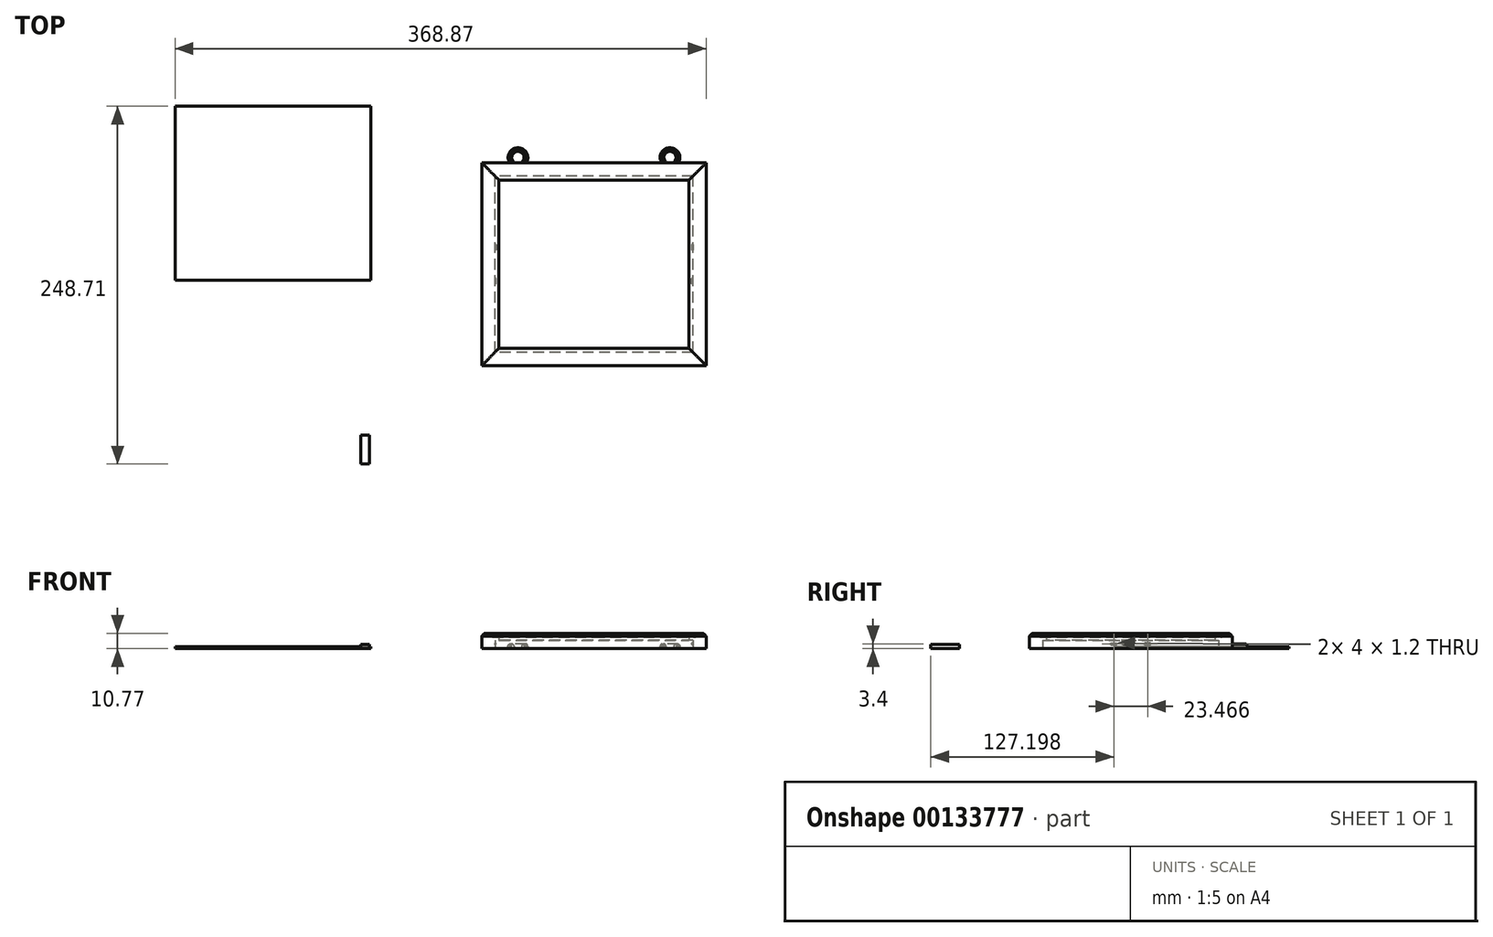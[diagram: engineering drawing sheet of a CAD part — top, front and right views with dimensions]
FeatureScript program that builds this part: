
annotation { "Feature Type Name" : "Feature", "Feature Type Description" : "" }
export const myFeature = defineFeature(function(context is Context, id is Id, definition is map)
    precondition{}
    {
        {
            var Q0;
            Q0=qCreatedBy(makeId("Top.planeOp"),FACE);
            var sketch = newSketch(context, id + "F0", { "sketchPlane" : qUnion([Q0])});
            skLineSegment(sketch, "E0.bottom", {"start": v(-66.53, 85.7) * mm, "end": v(11.47, 85.7) * mm});
            skLineSegment(sketch, "E0.top", {"start": v(-66.53, -55.3) * mm, "end": v(11.47, -55.3) * mm});
            skLineSegment(sketch, "E0.left", {"start": v(-66.53, 85.7) * mm, "end": v(-66.53, -55.3) * mm});
            skLineSegment(sketch, "E1.bottom", {"start": v(-54.53, 73.7) * mm, "end": v(11.47, 73.7) * mm});
            skLineSegment(sketch, "E1.top", {"start": v(-54.53, -43.3) * mm, "end": v(11.47, -43.3) * mm});
            skLineSegment(sketch, "E1.left", {"start": v(-54.53, 73.7) * mm, "end": v(-54.53, -43.3) * mm});
            skLineSegment(sketch, "E2", {"start": v(11.47, 73.7) * mm, "end": v(11.47, 85.7) * mm, "construction": true});
            skPoint(sketch, "E2.endSnap0", {"position": v(-27.53, 85.7) * mm});
            skLineSegment(sketch, "E3", {"start": v(11.47, -43.3) * mm, "end": v(11.47, -55.3) * mm, "construction": true});
            skLineSegment(sketch, "E4", {"start": v(-66.53, 15.2) * mm, "end": v(-54.53, 15.2) * mm, "construction": true});
            skLineSegment(sketch, "E5", {"start": v(11.47, 85.7) * mm, "end": v(11.47, -55.3) * mm});
            skSolve(sketch);
        }
        {
            var Q0;
            Q0=makeQuery(id+"F0.imprint","IMPRINT",FACE,{"disambiguationData":[TD([[makeQuery(id+"F0.imprint","IMPRINT",EDGE,{"derivedFrom":sQuery(id+"F0.wireOp",EDGE,"E0.bottom")}),-1.0]])]});
            extrude(context, id + "F1", {"entities" : qUnion([Q0]), "depth" : 11 * mm});
        }
        {
            var Q0;
            {var subQ0=sQuery(id+"F0.wireOp",EDGE,"E5");Q0=makeQuery(id+"F1.opExtrude","SWEPT_FACE",FACE,{"disambiguationData":[OSD([subQ0]),TDD([makeQuery(id+"F0.imprint","IMPRINT",EDGE,{"disambiguationData":[TD([[makeQuery(id+"F0.imprint","INTERSECT",VERTEX,{"derivedFrom":[sQuery(id+"F0.wireOp",EDGE,"E0.top"),subQ0]}),1.0]])],"derivedFrom":subQ0})])]});}
            var sketch = newSketch(context, id + "F2", { "sketchPlane" : qUnion([Q0])});
            skPoint(sketch, "E6.orphan", {"position": v(-55.3, 0) * mm});
            skPoint(sketch, "E7.orphan", {"position": v(-43.3, 0) * mm});
            skLineSegment(sketch, "E8.0", {"start": v(-43.3, 11) * mm, "end": v(-43.3, 9.78) * mm});
            skLineSegment(sketch, "E8.1", {"start": v(-43.3, 11) * mm, "end": v(-55.3, 11) * mm});
            skLineSegment(sketch, "E8.2", {"start": v(-55.3, 11) * mm, "end": v(-55.3, 8.58) * mm});
            skFitSpline(sketch, "E9", {"points": [v(-55.3, 8.58) * mm, v(-52.44, 10.76) * mm, v(-48.85, 8.44) * mm, v(-46.04, 8.62) * mm, v(-43.3, 9.78) * mm, v(-43.3, 9.83) * mm], "startDerivative": vector(9.21, 12.44) * mm, "endDerivative": vector(-0.8, 1.4) * mm});
            skSolve(sketch);
        }
        {
            var Q0;
            {var subQ0=sQuery(id+"F2.wireOp",EDGE,"E8.1");var subQ1=sQuery(id+"F2.wireOp",EDGE,"E8.0");var subQ2=makeQuery(id+"F2.imprint","INTERSECT",VERTEX,{"derivedFrom":[subQ1,subQ0]});Q0=makeQuery(id+"F2.imprint","IMPRINT",FACE,{"disambiguationData":[TD([[makeQuery(id+"F2.imprint","IMPRINT",EDGE,{"disambiguationData":[TD([[subQ2,-1.0]])],"derivedFrom":subQ1}),-1.0]])]});}
            var Q1;
            {var subQ0=sQuery(id+"F2.wireOp",EDGE,"E8.2");Q1=makeQuery(id+"F2.imprint","IMPRINT",FACE,{"disambiguationData":[TD([[makeQuery(id+"F2.imprint","IMPRINT",EDGE,{"derivedFrom":subQ0}),1.0]])]});}
            var Q2;
            Q2=makeQuery(id+"F1.opExtrude","CAP_EDGE",EDGE,{"disambiguationData":[OSD([sQuery(id+"F0.wireOp",EDGE,"E0.top")])],"isStart":false});
            var Q3;
            Q3=makeQuery(id+"F1.opExtrude","CAP_EDGE",EDGE,{"disambiguationData":[OSD([sQuery(id+"F0.wireOp",EDGE,"E0.left")])],"isStart":false});
            var Q4;
            Q4=makeQuery(id+"F1.opExtrude","CAP_EDGE",EDGE,{"disambiguationData":[OSD([sQuery(id+"F0.wireOp",EDGE,"E0.bottom")])],"isStart":false});
            sweep(context, id + "F3", {"operationType" : NewBodyOperationType.REMOVE, "profiles" : qUnion([Q0, Q1]), "path" : qUnion([Q2, Q3, Q4])});
        }
        {
            var Q0;
            Q0=makeQuery(id+"F1.opExtrude","CAP_FACE",FACE,{"disambiguationData":[OSD([sQuery(id+"F0.wireOp",EDGE,"E0.bottom"),sQuery(id+"F0.wireOp",EDGE,"E0.top"),sQuery(id+"F0.wireOp",EDGE,"E0.left"),sQuery(id+"F0.wireOp",EDGE,"E1.bottom"),sQuery(id+"F0.wireOp",EDGE,"E1.top"),sQuery(id+"F0.wireOp",EDGE,"E1.left"),sQuery(id+"F0.wireOp",EDGE,"E5")])],"isStart":true});
            var sketch = newSketch(context, id + "F4", { "sketchPlane" : qUnion([Q0])});
            skLineSegment(sketch, "E10.bottom", {"start": v(11.47, 46) * mm, "end": v(-57.23, 46) * mm});
            skLineSegment(sketch, "E10.top", {"start": v(11.47, -76.4) * mm, "end": v(-57.23, -76.4) * mm});
            skLineSegment(sketch, "E10.left", {"start": v(11.47, 46) * mm, "end": v(11.47, -76.4) * mm});
            skLineSegment(sketch, "E10.right", {"start": v(-57.23, 46) * mm, "end": v(-57.23, -76.4) * mm});
            skLineSegment(sketch, "E11", {"start": v(-50.93, 43.3) * mm, "end": v(-50.93, 46) * mm, "construction": true});
            skLineSegment(sketch, "E12", {"start": v(-54.53, 8.71) * mm, "end": v(-57.23, 8.71) * mm, "construction": true});
            skLineSegment(sketch, "E13", {"start": v(-42.3, -73.7) * mm, "end": v(-42.3, -76.4) * mm, "construction": true});
            skSolve(sketch);
        }
        {
            var Q0;
            {var subQ7=sQuery(id+"F4.wireOp",EDGE,"E10.bottom");Q0=makeQuery(id+"F4.imprint","IMPRINT",FACE,{"disambiguationData":[TD([[makeQuery(id+"F4.imprint","IMPRINT",EDGE,{"derivedFrom":subQ7}),1.0]])]});}
            extrude(context, id + "F5", {"entities" : qUnion([Q0]), "operationType" : NewBodyOperationType.REMOVE, "oppositeDirection" : true, "depth" : 6 * mm});
        }
        {
            var Q0;
            Q0=makeQuery(id+"F5.boolean.opBoolean","COPY",FACE,{"derivedFrom":makeQuery(id+"F5.opExtrude","SWEPT_FACE",FACE,{"disambiguationData":[OSD([sQuery(id+"F4.wireOp",EDGE,"E10.right")])]})});
            var sketch = newSketch(context, id + "F6", { "sketchPlane" : qUnion([Q0])});
            skLineSegment(sketch, "E14.bottom", {"start": v(1.46, 2.8) * mm, "end": v(5.46, 2.8) * mm});
            skLineSegment(sketch, "E14.top", {"start": v(1.46, 4) * mm, "end": v(5.46, 4) * mm});
            skLineSegment(sketch, "E14.left", {"start": v(1.46, 2.8) * mm, "end": v(1.46, 4) * mm});
            skLineSegment(sketch, "E14.right", {"start": v(5.46, 2.8) * mm, "end": v(5.46, 4) * mm});
            skLineSegment(sketch, "E15", {"start": v(15.2, 6) * mm, "end": v(15.2, 0) * mm, "construction": true});
            skLineSegment(sketch, "E16.MirrorCS", {"start": v(28.92, 2.8) * mm, "end": v(28.92, 4) * mm});
            skLineSegment(sketch, "E17.MirrorCS", {"start": v(24.92, 2.8) * mm, "end": v(24.92, 4) * mm});
            skLineSegment(sketch, "E18.MirrorCS", {"start": v(28.92, 2.8) * mm, "end": v(24.92, 2.8) * mm});
            skLineSegment(sketch, "E19.MirrorCS", {"start": v(28.92, 4) * mm, "end": v(24.92, 4) * mm});
            skSolve(sketch);
        }
        {
            var Q0;
            Q0 = qSketchRegion(id + "F6", true);
            extrude(context, id + "F7", {"entities" : qUnion([Q0]), "operationType" : NewBodyOperationType.ADD, "depth" : .7 * mm});
        }
        {
            var Q0;
            Q0=makeQuery(id+"F7.opExtrude","CAP_EDGE",EDGE,{"disambiguationData":[OSD([sQuery(id+"F6.wireOp",EDGE,"E14.bottom")])],"isStart":false});
            var Q1;
            Q1=makeQuery(id+"F7.opExtrude","CAP_EDGE",EDGE,{"disambiguationData":[OSD([sQuery(id+"F6.wireOp",EDGE,"E14.top")])],"isStart":false});
            var Q2;
            Q2=makeQuery(id+"F7.opExtrude","CAP_EDGE",EDGE,{"disambiguationData":[OSD([sQuery(id+"F6.wireOp",EDGE,"E18.MirrorCS")])],"isStart":false});
            var Q3;
            Q3=makeQuery(id+"F7.opExtrude","CAP_EDGE",EDGE,{"disambiguationData":[OSD([sQuery(id+"F6.wireOp",EDGE,"E19.MirrorCS")])],"isStart":false});
            fillet(context, id + "F8", {"entities" : qUnion([Q0, Q1, Q2, Q3]), "radius" : .4 * mm, "tangentPropagation" : true, "allowEdgeOverflow" : false});
        }
        {
            var Q0;
            Q0=makeQuery(id+"F1.opExtrude","SWEPT_BODY",BODY,{"disambiguationData":[OSD([sQuery(id+"F0.wireOp",EDGE,"E0.bottom"),sQuery(id+"F0.wireOp",EDGE,"E0.top"),sQuery(id+"F0.wireOp",EDGE,"E0.left"),sQuery(id+"F0.wireOp",EDGE,"E1.bottom"),sQuery(id+"F0.wireOp",EDGE,"E1.top"),sQuery(id+"F0.wireOp",EDGE,"E1.left"),sQuery(id+"F0.wireOp",EDGE,"E5")])]});
            var Q1;
            {var subQ0=sQuery(id+"F0.wireOp",EDGE,"E5");Q1=makeQuery(id+"F1.opExtrude","SWEPT_FACE",FACE,{"disambiguationData":[OSD([subQ0]),TDD([makeQuery(id+"F0.imprint","IMPRINT",EDGE,{"disambiguationData":[TD([[makeQuery(id+"F0.imprint","INTERSECT",VERTEX,{"derivedFrom":[sQuery(id+"F0.wireOp",EDGE,"E0.bottom"),subQ0]}),-1.0]])],"derivedFrom":subQ0})])]});}
            mirror(context, id + "F9", {"operationType" : NewBodyOperationType.ADD, "entities" : qUnion([Q0]), "mirrorPlane" : qUnion([Q1])});
        }
        {
            var Q0;
            Q0=qCreatedBy(makeId("Top.planeOp"),FACE);
            var sketch = newSketch(context, id + "F10", { "sketchPlane" : qUnion([Q0])});
            skLineSegment(sketch, "E20.bottom", {"start": v(-279.4, 124.97) * mm, "end": v(-143.4, 124.97) * mm});
            skLineSegment(sketch, "E20.top", {"start": v(-279.4, 3.97) * mm, "end": v(-143.4, 3.97) * mm});
            skLineSegment(sketch, "E20.left", {"start": v(-279.4, 124.97) * mm, "end": v(-279.4, 3.97) * mm});
            skLineSegment(sketch, "E20.right", {"start": v(-143.4, 124.97) * mm, "end": v(-143.4, 3.97) * mm});
            skSolve(sketch);
        }
        {
            var Q0;
            Q0=makeQuery(id+"F10.imprint","IMPRINT",FACE,{"disambiguationData":[TD([[makeQuery(id+"F10.imprint","IMPRINT",EDGE,{"derivedFrom":sQuery(id+"F10.wireOp",EDGE,"E20.bottom")}),-1.0]])]});
            extrude(context, id + "F11", {"entities" : qUnion([Q0]), "depth" : 1.4 * mm});
        }
        {
            var Q0;
            {var subQ0=makeQuery(id+"F1.opExtrude","CAP_FACE",FACE,{"disambiguationData":[OSD([sQuery(id+"F0.wireOp",EDGE,"E0.bottom"),sQuery(id+"F0.wireOp",EDGE,"E0.top"),sQuery(id+"F0.wireOp",EDGE,"E0.left"),sQuery(id+"F0.wireOp",EDGE,"E1.bottom"),sQuery(id+"F0.wireOp",EDGE,"E1.top"),sQuery(id+"F0.wireOp",EDGE,"E1.left"),sQuery(id+"F0.wireOp",EDGE,"E5")])],"isStart":true});Q0=makeQuery(id+"F9.boolean.opBoolean","MERGE",FACE,{"derivedFrom":[subQ0,makeQuery(id+"F9.opPattern","COPY",FACE,{"derivedFrom":subQ0,"instanceName":"1"})]});}
            var sketch = newSketch(context, id + "F12", { "sketchPlane" : qUnion([Q0])});
            skLineSegment(sketch, "E21", {"start": v(11.47, -85.7) * mm, "end": v(11.47, -73.3) * mm, "construction": true});
            skPoint(sketch, "E21.endSnap0", {"position": v(11.47, -76.4) * mm});
            skFitSpline(sketch, "E22", {"points": [v(66.83, -85.7) * mm, v(68.53, -90.13) * mm, v(64.25, -93.66) * mm, v(59.97, -90.13) * mm, v(61.67, -85.7) * mm], "startDerivative": vector(14.7, -15.41) * mm, "endDerivative": vector(12.67, 17.74) * mm});
            skPoint(sketch, "E23.orphan", {"position": v(89.47, -85.7) * mm});
            skLineSegment(sketch, "E24.trimOffspring", {"start": v(61.67, -85.7) * mm, "end": v(66.83, -85.7) * mm});
            skPoint(sketch, "E25.orphan", {"position": v(-66.53, -85.7) * mm});
            skLineSegment(sketch, "E26", {"start": v(59.97, -90.13) * mm, "end": v(64.25, -90.13) * mm, "construction": true});
            skLineSegment(sketch, "E27", {"start": v(64.25, -85.7) * mm, "end": v(64.25, -93.66) * mm, "construction": true});
            skLineSegment(sketch, "E28", {"start": v(64.25, -90.13) * mm, "end": v(68.53, -90.13) * mm, "construction": true});
            skFitSpline(sketch, "E29.0", {"points": [v(68.64, -83.97) * mm, v(69.02, -84.37) * mm, v(69.76, -85.25) * mm, v(70.53, -86.58) * mm, v(70.95, -87.83) * mm, v(71.13, -88.85) * mm, v(71.13, -89.75) * mm, v(71.02, -90.5) * mm, v(70.84, -91.23) * mm, v(70.5, -92.08) * mm, v(69.94, -93) * mm, v(69.27, -93.84) * mm, v(68.48, -94.58) * mm, v(67.6, -95.21) * mm, v(66.6, -95.72) * mm, v(65.66, -96.01) * mm, v(64.86, -96.14) * mm, v(64.23, -96.17) * mm, v(63.6, -96.13) * mm, v(62.81, -96) * mm, v(61.89, -95.7) * mm, v(60.9, -95.18) * mm, v(60, -94.54) * mm, v(59.22, -93.8) * mm, v(58.55, -92.98) * mm, v(58, -92.05) * mm, v(57.65, -91.2) * mm, v(57.48, -90.45) * mm, v(57.39, -89.7) * mm, v(57.42, -88.78) * mm, v(57.64, -87.79) * mm, v(58.1, -86.62) * mm, v(58.8, -85.41) * mm, v(59.37, -84.6) * mm, v(59.64, -84.24) * mm]});
            skLineSegment(sketch, "E30.MirrorCS", {"start": v(-38.74, -85.7) * mm, "end": v(-43.9, -85.7) * mm});
            skLineSegment(sketch, "E31.MirrorCS", {"start": v(-41.32, -90.13) * mm, "end": v(-45.6, -90.13) * mm, "construction": true});
            skLineSegment(sketch, "E32.MirrorCS", {"start": v(-37.04, -90.13) * mm, "end": v(-41.32, -90.13) * mm, "construction": true});
            skLineSegment(sketch, "E33.MirrorCS", {"start": v(-41.32, -85.7) * mm, "end": v(-41.32, -93.66) * mm, "construction": true});
            skFitSpline(sketch, "E34.MirrorCS", {"points": [v(-43.9, -85.7) * mm, v(-45.6, -90.13) * mm, v(-41.32, -93.66) * mm, v(-37.04, -90.13) * mm, v(-38.74, -85.7) * mm], "startDerivative": vector(-14.7, -15.41) * mm, "endDerivative": vector(-12.67, 17.74) * mm});
            skFitSpline(sketch, "E35.0", {"points": [v(-45.7, -83.97) * mm, v(-46.1, -84.37) * mm, v(-46.83, -85.25) * mm, v(-47.6, -86.58) * mm, v(-48.02, -87.83) * mm, v(-48.2, -88.85) * mm, v(-48.2, -89.75) * mm, v(-48.09, -90.5) * mm, v(-47.9, -91.23) * mm, v(-47.56, -92.08) * mm, v(-47, -93) * mm, v(-46.33, -93.84) * mm, v(-45.55, -94.58) * mm, v(-44.66, -95.21) * mm, v(-43.66, -95.72) * mm, v(-42.72, -96.01) * mm, v(-41.93, -96.14) * mm, v(-41.3, -96.17) * mm, v(-40.68, -96.13) * mm, v(-39.88, -96) * mm, v(-38.96, -95.7) * mm, v(-37.96, -95.18) * mm, v(-37.07, -94.54) * mm, v(-36.3, -93.8) * mm, v(-35.62, -92.98) * mm, v(-35.06, -92.05) * mm, v(-34.72, -91.2) * mm, v(-34.54, -90.45) * mm, v(-34.45, -89.7) * mm, v(-34.49, -88.78) * mm, v(-34.71, -87.79) * mm, v(-35.16, -86.62) * mm, v(-35.87, -85.41) * mm, v(-36.44, -84.6) * mm, v(-36.7, -84.24) * mm]});
            skSolve(sketch);
        }
        {
            var Q0;
            {var subQ0=sQuery(id+"F12.wireOp",EDGE,"E34.MirrorCS");Q0=makeQuery(id+"F12.imprint","IMPRINT",FACE,{"disambiguationData":[TD([[makeQuery(id+"F12.imprint","IMPRINT",EDGE,{"derivedFrom":subQ0}),-1.0]])]});}
            var Q1;
            {var subQ0=sQuery(id+"F12.wireOp",EDGE,"E22");Q1=makeQuery(id+"F12.imprint","IMPRINT",FACE,{"disambiguationData":[TD([[makeQuery(id+"F12.imprint","IMPRINT",EDGE,{"derivedFrom":subQ0}),1.0]])]});}
            var Q2;
            Q2=sQuery(id+"F12.wireOp",EDGE,"E22");
            var Q3;
            Q3=sQuery(id+"F12.wireOp",EDGE,"36efb535-0531-41de-a198-52480941e18c1.MirrorCS");
            extrude(context, id + "F13", {"entities" : qUnion([Q0, Q1]), "operationType" : NewBodyOperationType.ADD, "surfaceEntities" : qUnion([Q2, Q3]), "oppositeDirection" : true, "depth" : 3.5 * mm});
        }
        {
            var Q0;
            Q0=makeQuery(id+"F13.opExtrude","CAP_EDGE",EDGE,{"disambiguationData":[OSD([sQuery(id+"F12.wireOp",EDGE,"E29.0")])],"isStart":false});
            var Q1;
            Q1=makeQuery(id+"F13.opExtrude","CAP_EDGE",EDGE,{"disambiguationData":[OSD([sQuery(id+"F12.wireOp",EDGE,"E22")])],"isStart":false});
            var Q2;
            Q2=makeQuery(id+"F13.opExtrude","CAP_EDGE",EDGE,{"disambiguationData":[OSD([sQuery(id+"F12.wireOp",EDGE,"E35.0")])],"isStart":false});
            var Q3;
            Q3=makeQuery(id+"F13.opExtrude","CAP_EDGE",EDGE,{"disambiguationData":[OSD([sQuery(id+"F12.wireOp",EDGE,"E34.MirrorCS")])],"isStart":false});
            fillet(context, id + "F14", {"entities" : qUnion([Q0, Q1, Q2, Q3]), "radius" : 2 * mm, "tangentPropagation" : true, "allowEdgeOverflow" : false});
        }
        {
            var Q0;
            Q0=qCreatedBy(makeId("Top.planeOp"),FACE);
            var sketch = newSketch(context, id + "F15", { "sketchPlane" : qUnion([Q0])});
            skLineSegment(sketch, "E36.bottom", {"start": v(-150.61, -103.74) * mm, "end": v(-144.61, -103.74) * mm});
            skLineSegment(sketch, "E36.top", {"start": v(-150.61, -123.74) * mm, "end": v(-144.61, -123.74) * mm});
            skLineSegment(sketch, "E36.left", {"start": v(-150.61, -103.74) * mm, "end": v(-150.61, -123.74) * mm});
            skLineSegment(sketch, "E36.right", {"start": v(-144.61, -103.74) * mm, "end": v(-144.61, -123.74) * mm});
            skSolve(sketch);
        }
        {
            var Q0;
            Q0=makeQuery(id+"F15.imprint","IMPRINT",FACE,{"disambiguationData":[TD([[makeQuery(id+"F15.imprint","IMPRINT",EDGE,{"derivedFrom":sQuery(id+"F15.wireOp",EDGE,"E36.bottom")}),-1.0]])]});
            extrude(context, id + "F16", {"entities" : qUnion([Q0]), "depth" : 3 * mm});
        }
    });
